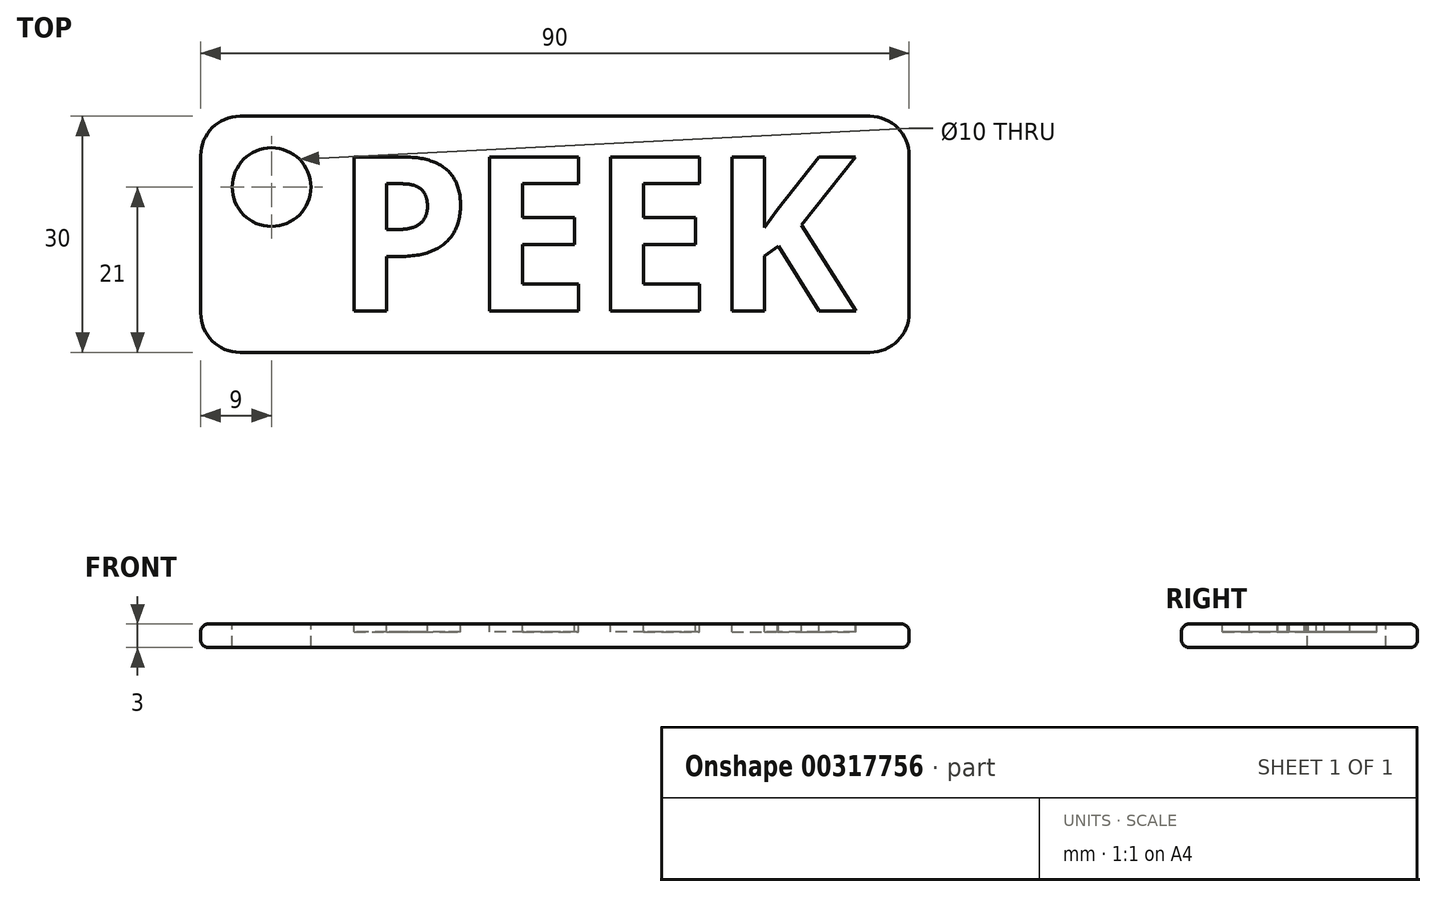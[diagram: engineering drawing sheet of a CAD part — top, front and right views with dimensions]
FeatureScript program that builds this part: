
annotation { "Feature Type Name" : "Feature", "Feature Type Description" : "" }
export const myFeature = defineFeature(function(context is Context, id is Id, definition is map)
    precondition{}
    {
        {
            var Q0;
            Q0=qCreatedBy(makeId("Top.planeOp"),FACE);
            var sketch = newSketch(context, id + "F0", { "sketchPlane" : qUnion([Q0])});
            skLineSegment(sketch, "E0.bottom", {"start": v(-45, 15) * mm, "end": v(45, 15) * mm});
            skLineSegment(sketch, "E0.top", {"start": v(-45, -15) * mm, "end": v(45, -15) * mm});
            skLineSegment(sketch, "E0.left", {"start": v(-45, 15) * mm, "end": v(-45, -15) * mm});
            skLineSegment(sketch, "E0.right", {"start": v(45, 15) * mm, "end": v(45, -15) * mm});
            skLineSegment(sketch, "E1", {"start": v(-45, 15) * mm, "end": v(45, -15) * mm, "construction": true});
            skSolve(sketch);
        }
        {
            var Q0;
            Q0=makeQuery(id+"F0.imprint","IMPRINT",FACE,{"disambiguationData":[TD([[makeQuery(id+"F0.imprint","IMPRINT",EDGE,{"derivedFrom":sQuery(id+"F0.wireOp",EDGE,"E0.bottom")}),-1.0]])]});
            extrude(context, id + "F1", {"entities" : qUnion([Q0]), "depth" : 3 * mm});
        }
        {
            var Q0;
            Q0=makeQuery(id+"F1.opExtrude","CAP_FACE",FACE,{"disambiguationData":[OSD([sQuery(id+"F0.wireOp",EDGE,"E0.bottom"),sQuery(id+"F0.wireOp",EDGE,"E0.top"),sQuery(id+"F0.wireOp",EDGE,"E0.left"),sQuery(id+"F0.wireOp",EDGE,"E0.right")])],"isStart":false});
            var Q1;
            Q1=makeQuery(id+"F1.opExtrude","CAP_FACE",FACE,{"disambiguationData":[OSD([sQuery(id+"F0.wireOp",EDGE,"E0.bottom"),sQuery(id+"F0.wireOp",EDGE,"E0.top"),sQuery(id+"F0.wireOp",EDGE,"E0.left"),sQuery(id+"F0.wireOp",EDGE,"E0.right")])],"isStart":true});
            fillet(context, id + "F2", {"entities" : qUnion([Q0, Q1]), "radius" : 1 * mm, "tangentPropagation" : true, "allowEdgeOverflow" : false});
        }
        {
            var Q0;
            Q0=makeQuery(id+"F1.opExtrude","SWEPT_EDGE",EDGE,{"disambiguationData":[OSD([sQuery(id+"F0.wireOp",EDGE,"E0.top"),sQuery(id+"F0.wireOp",EDGE,"E0.right")])]});
            var Q1;
            Q1=makeQuery(id+"F1.opExtrude","SWEPT_EDGE",EDGE,{"disambiguationData":[OSD([sQuery(id+"F0.wireOp",EDGE,"E0.bottom"),sQuery(id+"F0.wireOp",EDGE,"E0.right")])]});
            var Q2;
            Q2=makeQuery(id+"F1.opExtrude","SWEPT_EDGE",EDGE,{"disambiguationData":[OSD([sQuery(id+"F0.wireOp",EDGE,"E0.bottom"),sQuery(id+"F0.wireOp",EDGE,"E0.left")])]});
            var Q3;
            Q3=makeQuery(id+"F1.opExtrude","SWEPT_EDGE",EDGE,{"disambiguationData":[OSD([sQuery(id+"F0.wireOp",EDGE,"E0.top"),sQuery(id+"F0.wireOp",EDGE,"E0.left")])]});
            fillet(context, id + "F3", {"entities" : qUnion([Q0, Q1, Q2, Q3]), "radius" : 5 * mm, "tangentPropagation" : true, "allowEdgeOverflow" : false});
        }
        {
            var Q0;
            {var subQ0=sQuery(id+"F0.wireOp",EDGE,"E0.left");var subQ2=sQuery(id+"F0.wireOp",EDGE,"E0.bottom");var subQ4=sQuery(id+"F0.wireOp",EDGE,"E0.right");var subQ6=sQuery(id+"F0.wireOp",EDGE,"E0.top");Q0=makeQuery(id+"FmQCBBX3Ub0qneL_1.boolean.opBoolean","SPLIT",FACE,{"disambiguationData":[TD([makeQuery(id+"FmQCBBX3Ub0qneL_1.opExtrude","SWEPT_FACE",FACE,{"disambiguationData":[OSD([sQuery(id+"FOCoeRmDbjhRCuz_1.wireOp",EDGE,"4a1fb44a-e7be-4e23-9449-000d953c446c.sketch_text.stroke-0")])]})])],"derivedFrom":makeQuery(id+"F1.opExtrude","CAP_FACE",FACE,{"disambiguationData":[OSD([subQ2,subQ6,subQ0,subQ4])],"isStart":false})});}
            var sketch = newSketch(context, id + "F4", { "sketchPlane" : qUnion([Q0])});
            skCircle(sketch, "E2", {"center": v(-36, 6) * mm, "radius": 5 * mm});
            skSolve(sketch);
        }
        {
            var Q0;
            Q0=qSketchRegion(id+"F4",true);
            extrude(context, id + "F5", {"entities" : qUnion([Q0]), "operationType" : NewBodyOperationType.REMOVE, "oppositeDirection" : true, "depth" : 3 * mm});
        }
        {
            var Q0;
            Q0=makeQuery(id+"F1.opExtrude","CAP_FACE",FACE,{"disambiguationData":[OSD([sQuery(id+"F0.wireOp",EDGE,"E0.bottom"),sQuery(id+"F0.wireOp",EDGE,"E0.top"),sQuery(id+"F0.wireOp",EDGE,"E0.left"),sQuery(id+"F0.wireOp",EDGE,"E0.right")])],"isStart":false});
            var sketch = newSketch(context, id + "F6", { "sketchPlane" : qUnion([Q0])});
            skText(sketch, "E3", { "text": "PEEK", "fontName": "OpenSans-Bold.ttf"});
            const initialGuessF6  = {"E3": [-0.028, -0.00977, 1, 0, 0.01977]};
            skSetInitialGuess(sketch, initialGuessF6);
            skSolve(sketch);
        }
        {
            var Q0;
            Q0=qSketchRegion(id+"F6",true);
            extrude(context, id + "F7", {"entities" : qUnion([Q0]), "operationType" : NewBodyOperationType.REMOVE, "oppositeDirection" : true, "depth" : 1 * mm});
        }
    });
